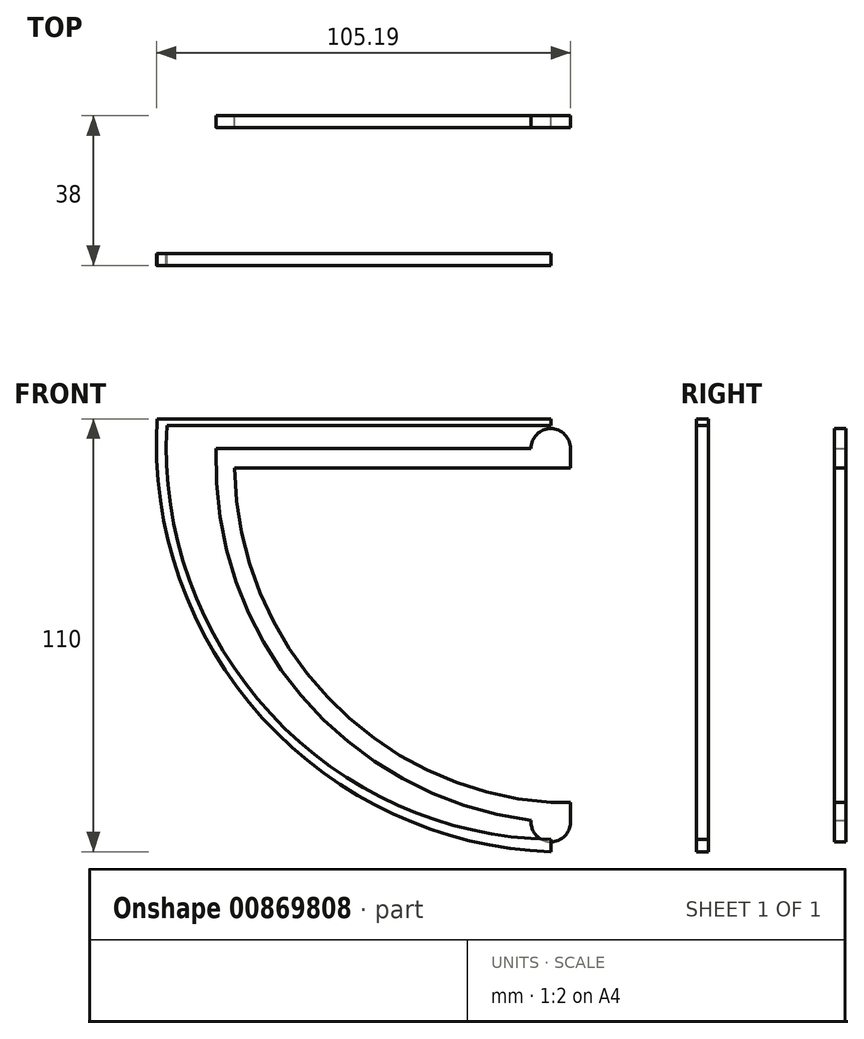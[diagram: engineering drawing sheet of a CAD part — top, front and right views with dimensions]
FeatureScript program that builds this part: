
annotation { "Feature Type Name" : "Feature", "Feature Type Description" : "" }
export const myFeature = defineFeature(function(context is Context, id is Id, definition is map)
    precondition{}
    {
        {
            var Q0;
            Q0=qCreatedBy(makeId("Front.planeOp"),FACE);
            var sketch = newSketch(context, id + "F0", { "sketchPlane" : qUnion([Q0])});
            skLineSegment(sketch, "E0", {"start": v(0, 47.5) * mm, "end": v(0, -42.5) * mm});
            skCircle(sketch, "E1", {"center": v(0, 47.5) * mm, "radius": 5 * mm});
            skCircle(sketch, "E2", {"center": v(0, -47.5) * mm, "radius": 5 * mm});
            skLineSegment(sketch, "E3", {"start": v(0, 47.5) * mm, "end": v(-85, 47.5) * mm});
            skArc(sketch, "E4", {"start": v(-85, 47.5) * mm, "mid": v(-61.76, -17.23) * mm, "end": v(0, -47.5) * mm});
            skLineSegment(sketch, "E5", {"start": v(0, 42.5) * mm, "end": v(-80.29, 42.5) * mm});
            skArc(sketch, "E6", {"start": v(-80.29, 42.5) * mm, "mid": v(-56.75, -15.69) * mm, "end": v(0, -42.5) * mm});
            skLineSegment(sketch, "E7", {"start": v(5, 47.5) * mm, "end": v(5, -47.5) * mm});
            skLineSegment(sketch, "E8", {"start": v(0, -47.5) * mm, "end": v(5, -47.5) * mm, "construction": true});
            skLineSegment(sketch, "E9", {"start": v(0, -42.5) * mm, "end": v(5, -42.5) * mm});
            skLineSegment(sketch, "E10", {"start": v(0, -47.5) * mm, "end": v(5, -47.5) * mm});
            skLineSegment(sketch, "E11", {"start": v(0, 47.5) * mm, "end": v(5, 47.5) * mm});
            skLineSegment(sketch, "E12", {"start": v(0, 42.5) * mm, "end": v(5, 42.5) * mm});
            skSolve(sketch);
        }
        {
            var Q0;
            Q0=qCreatedBy(makeId("Front.planeOp"),FACE);
            cPlane(context, id + "F1", {"entities" : qUnion([Q0]), "cplaneType" : CPlaneType.OFFSET, "offset" : 35 * mm, "width" : 150 * mm, "height" : 150 * mm});
        }
        {
            var Q0;
            Q0=qCreatedBy(id+"F1.planeOp",FACE);
            var sketch = newSketch(context, id + "F2", { "sketchPlane" : qUnion([Q0])});
            skLineSegment(sketch, "E13", {"start": v(0, 55) * mm, "end": v(0, -55) * mm});
            skLineSegment(sketch, "E14", {"start": v(0, 55) * mm, "end": v(-100, 55) * mm});
            skArc(sketch, "E15", {"start": v(-100, 55) * mm, "mid": v(-73.18, -21.07) * mm, "end": v(0, -55) * mm});
            skLineSegment(sketch, "E16", {"start": v(0, 53.32) * mm, "end": v(-97.53, 53.32) * mm});
            skArc(sketch, "E17", {"start": v(-97.53, 53.32) * mm, "mid": v(-71.11, -20) * mm, "end": v(0, -51.89) * mm});
            skSolve(sketch);
        }
        {
            var Q0;
            {var subQ1=sQuery(id+"F2.wireOp",EDGE,"E14");Q0=makeQuery(id+"F2.imprint","IMPRINT",FACE,{"disambiguationData":[TD([[makeQuery(id+"F2.imprint","IMPRINT",EDGE,{"derivedFrom":subQ1}),1.0]])]});}
            extrude(context, id + "F3", {"entities" : qUnion([Q0]), "depth" : 3 * mm, "offsetDistance" : 25 * mm});
        }
        {
            var Q0;
            {var subQ0=sQuery(id+"F0.wireOp",EDGE,"E11");Q0=makeQuery(id+"F0.imprint","IMPRINT",FACE,{"disambiguationData":[TD([[makeQuery(id+"F0.imprint","IMPRINT",EDGE,{"derivedFrom":subQ0}),1.0]])]});}
            var Q1;
            {var subQ0=sQuery(id+"F0.wireOp",EDGE,"E3");var subQ3=sQuery(id+"F0.wireOp",EDGE,"E1");var subQ5=makeQuery(id+"F0.imprint","INTERSECT",VERTEX,{"derivedFrom":[subQ3,subQ0]});Q1=makeQuery(id+"F0.imprint","IMPRINT",FACE,{"disambiguationData":[TD([[makeQuery(id+"F0.imprint","IMPRINT",EDGE,{"disambiguationData":[TD([[subQ5,1.0]])],"derivedFrom":subQ0}),1.0]])]});}
            var Q2;
            {var subQ0=sQuery(id+"F0.wireOp",EDGE,"E11");Q2=makeQuery(id+"F0.imprint","IMPRINT",FACE,{"disambiguationData":[TD([[makeQuery(id+"F0.imprint","IMPRINT",EDGE,{"derivedFrom":subQ0}),-1.0]])]});}
            var Q3;
            {var subQ9=sQuery(id+"F0.wireOp",EDGE,"E5");Q3=makeQuery(id+"F0.imprint","IMPRINT",FACE,{"disambiguationData":[TD([[makeQuery(id+"F0.imprint","IMPRINT",EDGE,{"derivedFrom":subQ9}),-1.0]])]});}
            var Q4;
            {var subQ2=sQuery(id+"F0.wireOp",EDGE,"E10");Q4=makeQuery(id+"F0.imprint","IMPRINT",FACE,{"disambiguationData":[TD([[makeQuery(id+"F0.imprint","IMPRINT",EDGE,{"derivedFrom":subQ2}),1.0]])]});}
            var Q5;
            {var subQ0=sQuery(id+"F0.wireOp",EDGE,"E10");Q5=makeQuery(id+"F0.imprint","IMPRINT",FACE,{"disambiguationData":[TD([[makeQuery(id+"F0.imprint","IMPRINT",EDGE,{"derivedFrom":subQ0}),-1.0]])]});}
            var Q6;
            {var subQ0=sQuery(id+"F0.wireOp",EDGE,"E9");Q6=makeQuery(id+"F0.imprint","IMPRINT",FACE,{"disambiguationData":[TD([[makeQuery(id+"F0.imprint","IMPRINT",EDGE,{"derivedFrom":subQ0}),-1.0]])]});}
            var Q7;
            {var subQ0=sQuery(id+"F0.wireOp",EDGE,"E12");Q7=makeQuery(id+"F0.imprint","IMPRINT",FACE,{"disambiguationData":[TD([[makeQuery(id+"F0.imprint","IMPRINT",EDGE,{"derivedFrom":subQ0}),1.0]])]});}
            extrude(context, id + "F4", {"entities" : qUnion([Q0, Q1, Q2, Q3, Q4, Q5, Q6, Q7]), "depth" : 3 * mm, "offsetDistance" : 25 * mm});
        }
        {
            var Q0;
            Q0=sQuery(id+"F0.wireOp",EDGE,"E6");
            var Q1;
            Q1=makeQuery(id+"F3.opExtrude","CAP_EDGE",EDGE,{"disambiguationData":[OSD([sQuery(id+"F2.wireOp",EDGE,"E17")])],"isStart":true});
            loft(context, id + "F5", {"bodyType" : ToolBodyType.SURFACE, "wireProfilesArray" : [{ "wireProfileEntities" : qUnion([Q0]) }, { "wireProfileEntities" : qUnion([Q1]) }]});
        }
        {
            var Q0;
            Q0=makeQuery(id+"F3.opExtrude","CAP_EDGE",EDGE,{"disambiguationData":[OSD([sQuery(id+"F2.wireOp",EDGE,"E15")])],"isStart":true});
            var Q1;
            Q1=makeQuery(id+"F4.opExtrude","CAP_EDGE",EDGE,{"disambiguationData":[OSD([sQuery(id+"F0.wireOp",EDGE,"E4")])],"isStart":false});
            loft(context, id + "F6", {"bodyType" : ToolBodyType.SURFACE, "wireProfilesArray" : [{ "wireProfileEntities" : qUnion([Q0]) }, { "wireProfileEntities" : qUnion([Q1]) }]});
        }
        {
            var Q0;
            Q0=makeQuery(id+"F4.opExtrude","CAP_EDGE",EDGE,{"disambiguationData":[OSD([sQuery(id+"F0.wireOp",EDGE,"E3")])],"isStart":false});
            var Q1;
            Q1=makeQuery(id+"F3.opExtrude","CAP_EDGE",EDGE,{"disambiguationData":[OSD([sQuery(id+"F2.wireOp",EDGE,"E14")])],"isStart":true});
            loft(context, id + "F7", {"bodyType" : ToolBodyType.SURFACE, "wireProfilesArray" : [{ "wireProfileEntities" : qUnion([Q0]) }, { "wireProfileEntities" : qUnion([Q1]) }]});
        }
        {
            var Q0;
            Q0=makeQuery(id+"F4.opExtrude","CAP_EDGE",EDGE,{"disambiguationData":[OSD([sQuery(id+"F0.wireOp",EDGE,"E5"),sQuery(id+"F0.wireOp",EDGE,"E12")])],"isStart":false});
            var Q1;
            Q1=makeQuery(id+"F3.opExtrude","CAP_EDGE",EDGE,{"disambiguationData":[OSD([sQuery(id+"F2.wireOp",EDGE,"E16")])],"isStart":true});
            loft(context, id + "F8", {"bodyType" : ToolBodyType.SURFACE, "wireProfilesArray" : [{ "wireProfileEntities" : qUnion([Q0]) }, { "wireProfileEntities" : qUnion([Q1]) }]});
        }
    });
